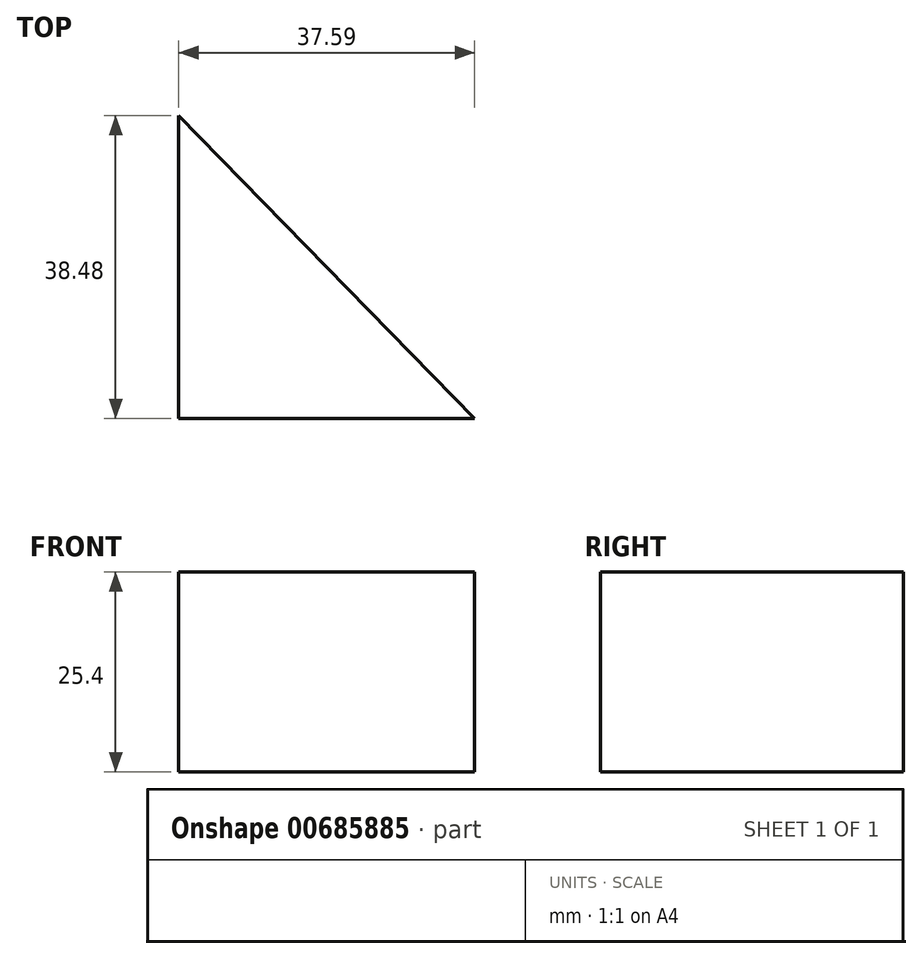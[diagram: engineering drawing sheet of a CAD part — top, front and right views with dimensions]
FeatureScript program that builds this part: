
annotation { "Feature Type Name" : "Feature", "Feature Type Description" : "" }
export const myFeature = defineFeature(function(context is Context, id is Id, definition is map)
    precondition{}
    {
        {
            var Q0;
            Q0=qCreatedBy(makeId("Top.planeOp"),FACE);
            var sketch = newSketch(context, id + "F0", { "sketchPlane" : qUnion([Q0])});
            skLineSegment(sketch, "E0", {"start": v(0, 0) * mm, "end": v(-37.59, 0) * mm});
            skLineSegment(sketch, "E1", {"start": v(-37.59, 38.48) * mm, "end": v(-37.59, 0) * mm});
            skLineSegment(sketch, "E2", {"start": v(-37.59, 38.48) * mm, "end": v(0, 0) * mm});
            skSolve(sketch);
        }
        {
            var Q0;
            Q0 = qSketchRegion(id + "F0", true);
            extrude(context, id + "F1", {"entities" : qUnion([Q0]), "depth" : 25.4 * mm, "offsetDistance" : 25.4 * mm});
        }
    });
